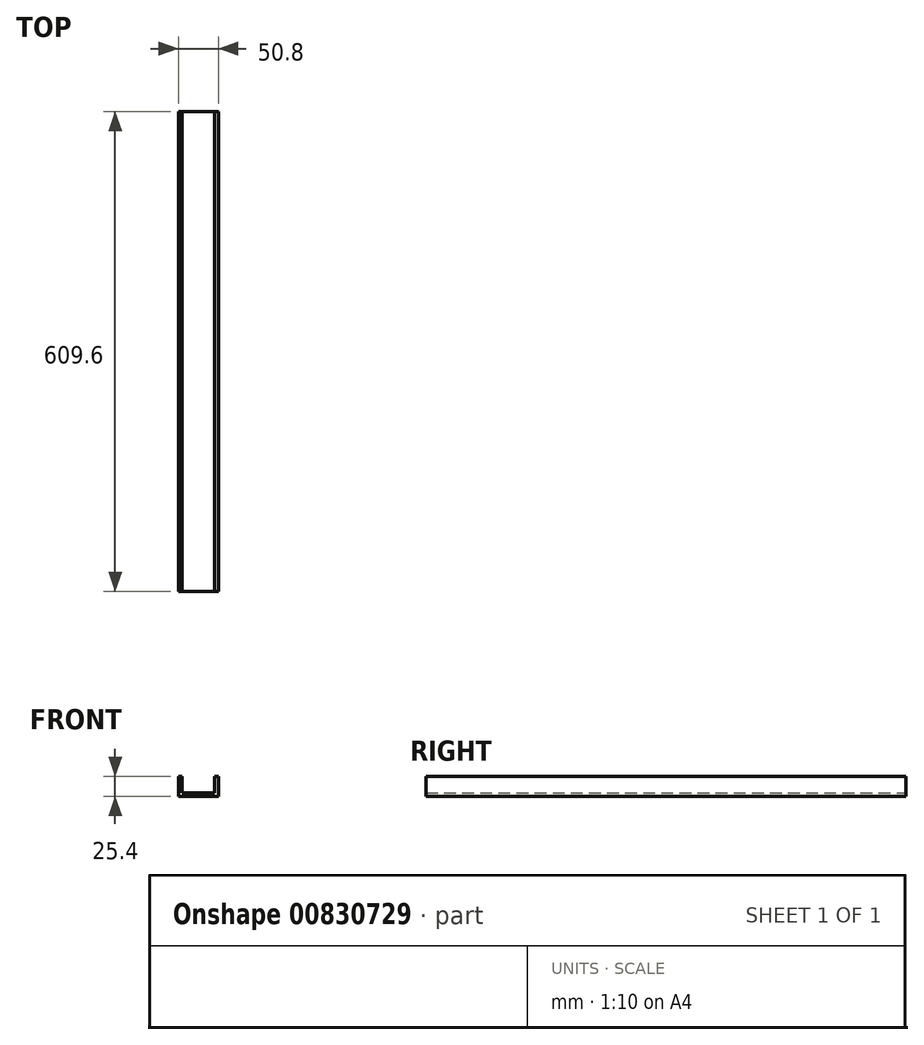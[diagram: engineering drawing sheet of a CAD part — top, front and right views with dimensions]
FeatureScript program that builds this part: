
annotation { "Feature Type Name" : "Feature", "Feature Type Description" : "" }
export const myFeature = defineFeature(function(context is Context, id is Id, definition is map)
    precondition{}
    {
        {
            var Q0;
            Q0=qCreatedBy(makeId("Front.planeOp"),FACE);
            var sketch = newSketch(context, id + "F0", { "sketchPlane" : qUnion([Q0])});
            skLineSegment(sketch, "E0.bottom", {"start": v(-25.4, 0) * mm, "end": v(25.4, 0) * mm});
            skLineSegment(sketch, "E0.top", {"start": v(-25.4, 25.4) * mm, "end": v(-20.64, 25.4) * mm});
            skLineSegment(sketch, "E0.left", {"start": v(-25.4, 0) * mm, "end": v(-25.4, 25.4) * mm});
            skLineSegment(sketch, "E0.right", {"start": v(25.4, 0) * mm, "end": v(25.4, 25.4) * mm});
            skLineSegment(sketch, "E1.top", {"start": v(-20.64, 4.76) * mm, "end": v(20.64, 4.76) * mm});
            skLineSegment(sketch, "E1.left", {"start": v(-20.64, 25.4) * mm, "end": v(-20.64, 4.76) * mm});
            skLineSegment(sketch, "E1.right", {"start": v(20.64, 25.4) * mm, "end": v(20.64, 4.76) * mm});
            skLineSegment(sketch, "E2.trimOffspring", {"start": v(20.64, 25.4) * mm, "end": v(25.4, 25.4) * mm});
            skSolve(sketch);
        }
        {
            var Q0;
            Q0 = qSketchRegion(id + "F0", true);
            extrude(context, id + "F1", {"entities" : qUnion([Q0]), "endBound" : BoundingType.SYMMETRIC, "depth" : 609.6 * mm, "offsetDistance" : 25.4 * mm});
        }
    });
